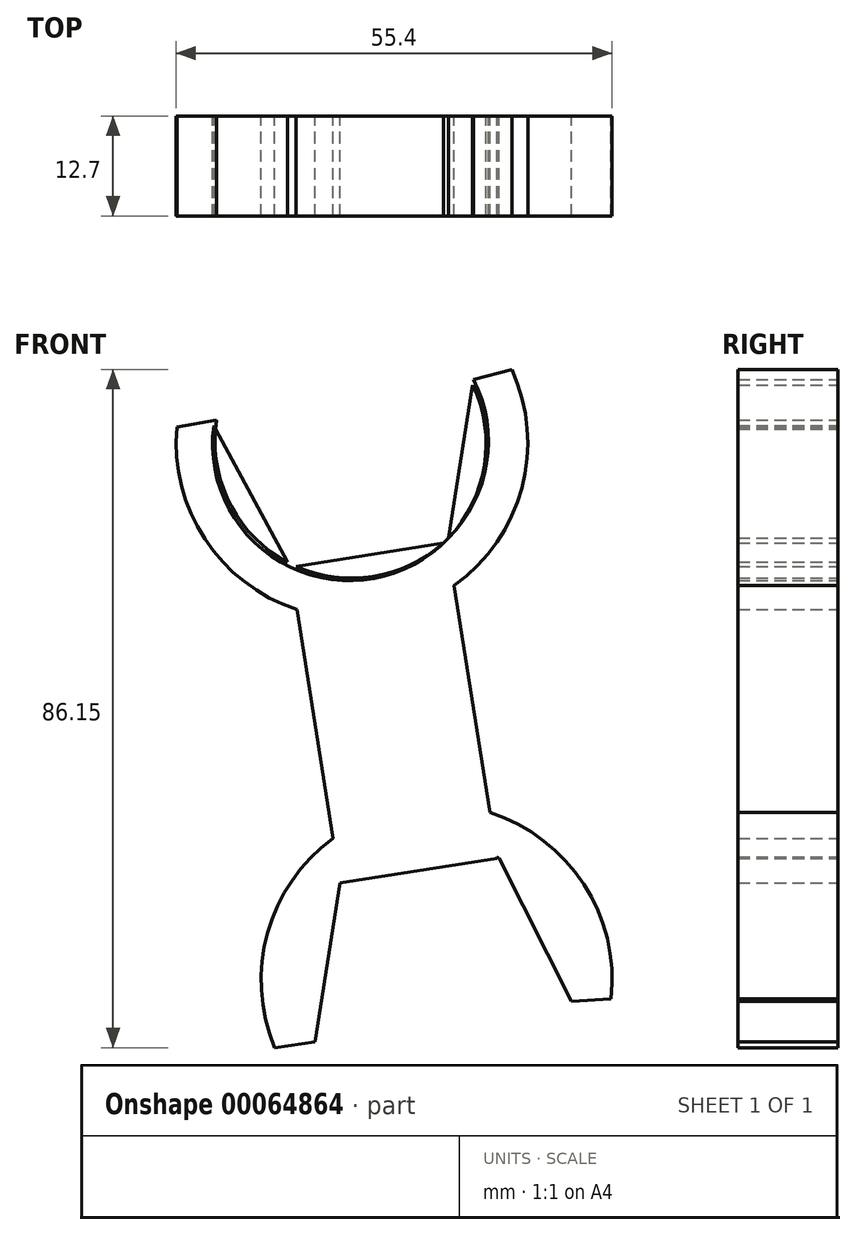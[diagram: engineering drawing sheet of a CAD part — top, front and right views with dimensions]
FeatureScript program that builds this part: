
annotation { "Feature Type Name" : "Feature", "Feature Type Description" : "" }
export const myFeature = defineFeature(function(context is Context, id is Id, definition is map)
    precondition{}
    {
        {
            var Q0;
            Q0=qCreatedBy(makeId("Front.planeOp"),FACE);
            var sketch = newSketch(context, id + "F0", { "sketchPlane" : qUnion([Q0])});
            skLineSegment(sketch, "E0", {"start": v(-28.85, 1.56) * mm, "end": v(-35.19, 41.7) * mm});
            skLineSegment(sketch, "E1", {"start": v(-55.13, 38.55) * mm, "end": v(-48.8, -1.6) * mm});
            skCircle(sketch, "E2.cCircle", {"center": v(-36.53, -13.88) * mm, "radius": 14.05 * mm, "construction": true});
            skLineSegment(sketch, "E2.0", {"start": v(-48.8, -1.6) * mm, "end": v(-28.64, 1.6) * mm});
            skLineSegment(sketch, "E2.1", {"start": v(-28.64, 1.6) * mm, "end": v(-19.38, -16.6) * mm});
            skLineSegment(sketch, "E2.4", {"start": v(-52, -21.75) * mm, "end": v(-48.8, -1.6) * mm});
            skPoint(sketch, "E2.0.midPoint", {"position": v(-38.72, 0) * mm});
            skLineSegment(sketch, "E3", {"start": v(-35.19, 41.7) * mm, "end": v(-55.13, 38.55) * mm});
            skArc(sketch, "E4", {"start": v(-19.38, -16.6) * mm, "mid": v(-39.23, 3.28) * mm, "end": v(-52, -21.75) * mm});
            skPoint(sketch, "E5.orphan", {"position": v(-33.82, -31.03) * mm});
            skLineSegment(sketch, "E6", {"start": v(-52, 18.73) * mm, "end": v(-32.06, 21.88) * mm, "construction": true});
            skLineSegment(sketch, "E7.MirrorCS", {"start": v(-55.21, 39.05) * mm, "end": v(-35.05, 42.23) * mm});
            skPoint(sketch, "E8.MirrorP", {"position": v(-50.02, 71.67) * mm});
            skPoint(sketch, "E9.MirrorP", {"position": v(-45.13, 40.64) * mm});
            skCircle(sketch, "E10.cCircle", {"center": v(-47.62, 54.21) * mm, "radius": 17.37 * mm, "construction": true});
            skLineSegment(sketch, "E10.0", {"start": v(-35.05, 42.23) * mm, "end": v(-55.13, 38.55) * mm});
            skLineSegment(sketch, "E10.1", {"start": v(-55.13, 38.55) * mm, "end": v(-64.84, 56.52) * mm});
            skLineSegment(sketch, "E10.4", {"start": v(-32.34, 62.47) * mm, "end": v(-35.05, 42.23) * mm});
            skArc(sketch, "E11", {"start": v(-64.84, 56.52) * mm, "mid": v(-44.5, 37.13) * mm, "end": v(-32.34, 62.47) * mm});
            skArc(sketch, "E12", {"start": v(-14.37, -16.32) * mm, "mid": v(-39.71, 8.2) * mm, "end": v(-57.1, -22.49) * mm});
            skLineSegment(sketch, "E13", {"start": v(-57.1, -22.49) * mm, "end": v(-52, -21.75) * mm});
            skLineSegment(sketch, "E14", {"start": v(-19.38, -16.6) * mm, "end": v(-14.37, -16.32) * mm});
            skLineSegment(sketch, "E15.MirrorCS", {"start": v(-31.84, 62.39) * mm, "end": v(-26.99, 63.66) * mm});
            skLineSegment(sketch, "E16.MirrorCS", {"start": v(-69.54, 56.38) * mm, "end": v(-64.47, 57.24) * mm});
            skLineSegment(sketch, "E17.MirrorCS", {"start": v(-35.05, 42.23) * mm, "end": v(-31.84, 62.39) * mm});
            skArc(sketch, "E18.MirrorCS", {"start": v(-31.84, 62.39) * mm, "mid": v(-44.61, 37.36) * mm, "end": v(-64.47, 57.24) * mm});
            skLineSegment(sketch, "E19.MirrorCS", {"start": v(-64.47, 57.24) * mm, "end": v(-55.21, 39.05) * mm});
            skCircle(sketch, "E20.MirrorC", {"center": v(-47.32, 54.51) * mm, "radius": 14.05 * mm, "construction": true});
            skArc(sketch, "E21", {"start": v(-69.54, 56.38) * mm, "mid": v(-43.52, 32.36) * mm, "end": v(-26.99, 63.66) * mm});
            skSolve(sketch);
        }
        {
            var Q0;
            {var subQ0=sQuery(id+"F0.wireOp",EDGE,"E12");var subQ1=sQuery(id+"F0.wireOp",EDGE,"E0");var subQ2=makeQuery(id+"F0.imprint","INTERSECT",VERTEX,{"derivedFrom":[subQ1,subQ0]});Q0=makeQuery(id+"F0.imprint","IMPRINT",FACE,{"disambiguationData":[TD([[makeQuery(id+"F0.imprint","IMPRINT",EDGE,{"disambiguationData":[TD([[subQ2,-1.0]])],"derivedFrom":subQ1}),1.0]])]});}
            var Q1;
            {var subQ1=sQuery(id+"F0.wireOp",EDGE,"E3");var subQ5=sQuery(id+"F0.wireOp",EDGE,"E0");var subQ6=makeQuery(id+"F0.imprint","INTERSECT",VERTEX,{"derivedFrom":[subQ5,subQ1]});Q1=makeQuery(id+"F0.imprint","IMPRINT",FACE,{"disambiguationData":[TD([[makeQuery(id+"F0.imprint","IMPRINT",EDGE,{"disambiguationData":[TD([[subQ6,1.0]])],"derivedFrom":subQ5}),1.0]])]});}
            var Q2;
            {var subQ0=sQuery(id+"F0.wireOp",EDGE,"E16.MirrorCS");Q2=makeQuery(id+"F0.imprint","IMPRINT",FACE,{"disambiguationData":[TD([[makeQuery(id+"F0.imprint","IMPRINT",EDGE,{"derivedFrom":subQ0}),-1.0]])]});}
            var Q3;
            {var subQ0=sQuery(id+"F0.wireOp",EDGE,"E18.MirrorCS");var subQ1=sQuery(id+"F0.wireOp",EDGE,"E10.1");var subQ2=makeQuery(id+"F0.imprint","INTERSECT",VERTEX,{"disambiguationData":[OD(0.0)],"derivedFrom":[subQ1,subQ0]});Q3=makeQuery(id+"F0.imprint","IMPRINT",FACE,{"disambiguationData":[TD([[makeQuery(id+"F0.imprint","IMPRINT",EDGE,{"disambiguationData":[TD([[subQ2,-1.0]])],"derivedFrom":subQ1}),1.0]])]});}
            var Q4;
            {var subQ0=sQuery(id+"F0.wireOp",EDGE,"E17.MirrorCS");var subQ1=sQuery(id+"F0.wireOp",EDGE,"E11");var subQ3=makeQuery(id+"F0.imprint","INTERSECT",VERTEX,{"derivedFrom":[subQ1,subQ0]});Q4=makeQuery(id+"F0.imprint","IMPRINT",FACE,{"disambiguationData":[TD([[makeQuery(id+"F0.imprint","IMPRINT",EDGE,{"disambiguationData":[TD([[subQ3,1.0]])],"derivedFrom":subQ1}),1.0]])]});}
            var Q5;
            {var subQ0=sQuery(id+"F0.wireOp",EDGE,"E15.MirrorCS");Q5=makeQuery(id+"F0.imprint","IMPRINT",FACE,{"disambiguationData":[TD([[makeQuery(id+"F0.imprint","IMPRINT",EDGE,{"derivedFrom":subQ0}),-1.0]])]});}
            var Q6;
            {var subQ6=sQuery(id+"F0.wireOp",EDGE,"E13");Q6=makeQuery(id+"F0.imprint","IMPRINT",FACE,{"disambiguationData":[TD([[makeQuery(id+"F0.imprint","IMPRINT",EDGE,{"derivedFrom":subQ6}),1.0]])]});}
            var Q7;
            {var subQ0=sQuery(id+"F0.wireOp",EDGE,"E2.4");Q7=makeQuery(id+"F0.imprint","IMPRINT",FACE,{"disambiguationData":[TD([[makeQuery(id+"F0.imprint","IMPRINT",EDGE,{"derivedFrom":subQ0}),1.0]])]});}
            var Q8;
            {var subQ0=sQuery(id+"F0.wireOp",EDGE,"E18.MirrorCS");var subQ1=sQuery(id+"F0.wireOp",EDGE,"E3");var subQ2=makeQuery(id+"F0.imprint","INTERSECT",VERTEX,{"disambiguationData":[OD(0.0)],"derivedFrom":[subQ1,subQ0]});Q8=makeQuery(id+"F0.imprint","IMPRINT",FACE,{"disambiguationData":[TD([[makeQuery(id+"F0.imprint","IMPRINT",EDGE,{"disambiguationData":[TD([[subQ2,-1.0]])],"derivedFrom":subQ1}),1.0]])]});}
            var Q9;
            {var subQ0=sQuery(id+"F0.wireOp",EDGE,"E2.1");Q9=makeQuery(id+"F0.imprint","IMPRINT",FACE,{"disambiguationData":[TD([[makeQuery(id+"F0.imprint","IMPRINT",EDGE,{"derivedFrom":subQ0}),1.0]])]});}
            var Q10;
            {var subQ0=sQuery(id+"F0.wireOp",EDGE,"E14");Q10=makeQuery(id+"F0.imprint","IMPRINT",FACE,{"disambiguationData":[TD([[makeQuery(id+"F0.imprint","IMPRINT",EDGE,{"derivedFrom":subQ0}),1.0]])]});}
            var Q11;
            {var subQ0=sQuery(id+"F0.wireOp",EDGE,"E12");var subQ1=sQuery(id+"F0.wireOp",EDGE,"E0");var subQ2=makeQuery(id+"F0.imprint","INTERSECT",VERTEX,{"derivedFrom":[subQ1,subQ0]});Q11=makeQuery(id+"F0.imprint","IMPRINT",FACE,{"disambiguationData":[TD([[makeQuery(id+"F0.imprint","IMPRINT",EDGE,{"disambiguationData":[TD([[subQ2,1.0]])],"derivedFrom":subQ1}),1.0]])]});}
            var Q12;
            {var subQ0=sQuery(id+"F0.wireOp",EDGE,"E2.0");var subQ1=sQuery(id+"F0.wireOp",EDGE,"E0");var subQ2=makeQuery(id+"F0.imprint","INTERSECT",VERTEX,{"derivedFrom":[subQ1,subQ0]});Q12=makeQuery(id+"F0.imprint","IMPRINT",FACE,{"disambiguationData":[TD([[makeQuery(id+"F0.imprint","IMPRINT",EDGE,{"disambiguationData":[TD([[subQ2,-1.0]])],"derivedFrom":subQ1}),1.0]])]});}
            extrude(context, id + "F1", {"entities" : qUnion([Q0, Q1, Q2, Q3, Q4, Q5, Q6, Q7, Q8, Q9, Q10, Q11, Q12]), "depth" : 12.7 * mm});
        }
    });
